# Revit family: PlumbingFixture_Grate_Galvin_GC100V-Slip
name_source: partatom
category: Plumbing Fixtures
revit_build: Autodesk Revit MEP 2012 (Build: 20110916_2132(x64)
units: mm (PartAtom-declared; Revit-internal decimal feet)

## types (1)
- 69457X - ST/ST 316
    Application = PVC
    Assembly Code = D2040200
    CHWFlow_ANZRS = 2.8 L/s
    Circulation_ANZRS = Yes
    Default Elevation = 0 mm  [stored 0 ft]
    Description = Vinyl Slip-In Slip-Safe ®  Bolted Cleanout Assembly
    DimDepth = 25 mm  [stored 0.082021 ft]
    DimHeight = 53 mm  [stored 0.173885 ft]
    DimOutlet = 80 mm  [stored 0.262467 ft]
    DimTop = 100 mm  [stored 0.328084 ft]
    FilterObject_ANZRS = GC-Slip
    GrateMaterial = Metal_Drains_Stainless-Steel_15400
    Instructions = http://www.galvinengineering.com.au
    Keynote = 10800
    Manufacturer = Galvin Engineering
    Model = 69457X - ST/ST 316
    ModifiedIssue_ANZRS = 20140526 $
    OutletRadius_DoNotEdit = 40 mm  [stored 0.131234 ft]
    StyleOrType_ANZRS = Grate
    Type Comments = Round
    URL = www.galvinengineering.com.au

note: [stored X ft] marks values corroborated as IEEE doubles in the binary element streams (Revit-internal decimal feet)

## geometry (parser evidence)
native form markers: Blend x2, Sweep x1
no freeform markers — native parametric forms only
